# Revit family: Soap_Dispenser-Bobrick-B-2111
name_source: partatom
category: Specialty Equipment
revit_build: Autodesk Revit 2014 (Build: 20130308_1515(x64)
units: mm (PartAtom-declared; Revit-internal decimal feet)

## types (1)
- B-2111
    ADA Compliant = Yes
    Assembly Code = E1010
    Default Elevation = 46 13/16"
    Description = ClassicSeries® Surface-Mounted Soap Dispenser
    Height = 8 1/8"
    Installation Type = Secure wall plate to the wall with three sheet-metal screws, furnished by manufacturer, at points indicated by an S. Slide mounting bracket of container down onto wall plate and secure unit with furnished locking-screw. For plaster or dry wall construction, provide concealed backing to comply with local building codes and secure with sheet-metal screws furnished. For other wall surfaces, provide fiber plugs or expansion shields for use with sheet-metal screws furnished, or provide 1/8" (3mm) toggle bolts or expansion bolts. Note: Surface-mount the dispenser plumb and true with valve 6'' (150mm) to right or left of lavatory center. Provide 4'' (100mm) minimum clearance from the lid to the underside of any horizontal projection. Push buttons should be located 44" (1120mm) maximum above the finish floor.
    Length = 3 1/2"
    Manufacturer = Bobrick
    Material = Stainless Steel-Bobrick-Type 304-Satin
    Model = B-2111
    Operation = Corrosion-resistant valve dispenses commercially marketed all-purpose hand soaps. To prevent corrosion of the tank, use only chloride-free pH-neutral liquid soaps. Valve is operable with one hand, without tight grasping, pinching, or twisting of the wrist, and with less than 5 pounds of force (22.2 N) to comply with accessible design guidelines (including ADAAG in the U.S.A.). Window indicates when refill is required. The locked, hinged lid opens for top filling only with special key provided. Concealed, vandal-resistant mounting.
    Product Documentation Link = http://www.bobrick.com
    Product URL = http://www.bobrick.com
    Specification = Surface-mounted soap dispenser shall be Type-304 stainless steel with satin-finish. Corrosion-resistant valve shall dispense commercially marketed all-purpose hand soaps, non-iodine based soaps and do not use alcohol based   sensitizers. To prevent corrosion of the tank, use only chloride-free pH-neutral liquid soaps. Valve shall be operable with one hand and with less than 5 pounds of force (22.2 N) to comply with accessible design guidelines (including ADAAG in the U.S.A.). Container shall be equipped with a clear acrylic refill-indicator window; a locked, hinged stainless steel lid for top filling; and shall have a capacity of 40-fl oz (1.2-L). Unit shall have concealed, vandal-resistant mounting.
    URL = http://www.bobrick.com
    Width = 4 3/4"

## geometry (parser evidence)
native form markers: Sweep x1
no freeform markers — native parametric forms only
